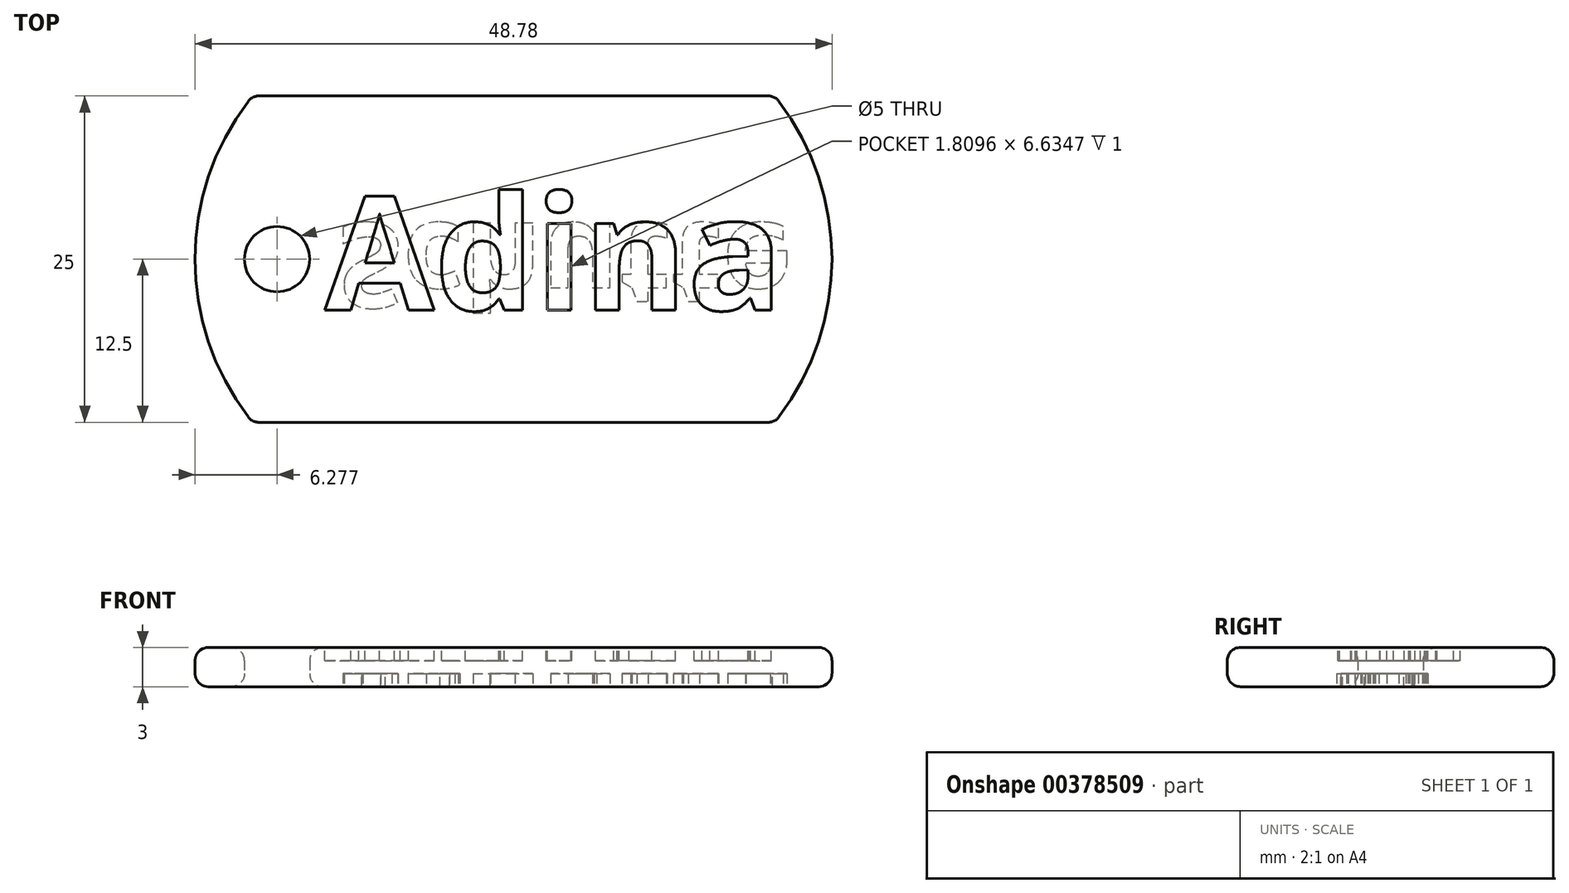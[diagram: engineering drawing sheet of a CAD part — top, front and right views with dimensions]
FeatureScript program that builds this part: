
annotation { "Feature Type Name" : "Feature", "Feature Type Description" : "" }
export const myFeature = defineFeature(function(context is Context, id is Id, definition is map)
    precondition{}
    {
        {
            var Q0;
            Q0=qCreatedBy(makeId("Top.planeOp"),FACE);
            var sketch = newSketch(context, id + "F0", { "sketchPlane" : qUnion([Q0])});
            skLineSegment(sketch, "E0.bottom", {"start": v(-20, 12.5) * mm, "end": v(20, 12.5) * mm});
            skLineSegment(sketch, "E0.top", {"start": v(-20, -12.5) * mm, "end": v(20, -12.5) * mm});
            skArc(sketch, "E1", {"start": v(-20, 12.5) * mm, "mid": v(-24.39, 0) * mm, "end": v(-20, -12.5) * mm});
            skArc(sketch, "E2", {"start": v(20, -12.5) * mm, "mid": v(24.39, 0) * mm, "end": v(20, 12.5) * mm});
            skCircle(sketch, "E3", {"center": v(-18.11, 0) * mm, "radius": 2.5 * mm});
            skSolve(sketch);
        }
        {
            var Q0;
            Q0=makeQuery(id+"F0.imprint","IMPRINT",FACE,{"disambiguationData":[TD([[makeQuery(id+"F0.imprint","IMPRINT",EDGE,{"derivedFrom":sQuery(id+"F0.wireOp",EDGE,"E0.bottom")}),-1.0]])]});
            extrude(context, id + "F1", {"entities" : qUnion([Q0]), "depth" : 3 * mm});
        }
        {
            var Q0;
            Q0=makeQuery(id+"F1.opExtrude","CAP_FACE",FACE,{"disambiguationData":[OSD([sQuery(id+"F0.wireOp",EDGE,"E0.bottom"),sQuery(id+"F0.wireOp",EDGE,"E0.top"),sQuery(id+"F0.wireOp",EDGE,"E1"),sQuery(id+"F0.wireOp",EDGE,"E2"),sQuery(id+"F0.wireOp",EDGE,"E3")])],"isStart":false});
            var sketch = newSketch(context, id + "F2", { "sketchPlane" : qUnion([Q0])});
            skText(sketch, "E4", { "text": "Adina\n", "fontName": "OpenSans-Bold.ttf"});
            const initialGuessF2  = {"E4": [-0.01445, -0.0039, 1, 0, 0.00875]};
            skSetInitialGuess(sketch, initialGuessF2);
            skSolve(sketch);
        }
        {
            var Q0;
            Q0=qSketchRegion(id+"F2",true);
            extrude(context, id + "F3", {"entities" : qUnion([Q0]), "operationType" : NewBodyOperationType.REMOVE, "oppositeDirection" : true, "depth" : 1 * mm});
        }
        {
            var Q0;
            Q0=makeQuery(id+"F1.opExtrude","CAP_FACE",FACE,{"disambiguationData":[OSD([sQuery(id+"F0.wireOp",EDGE,"E0.bottom"),sQuery(id+"F0.wireOp",EDGE,"E0.top"),sQuery(id+"F0.wireOp",EDGE,"E1"),sQuery(id+"F0.wireOp",EDGE,"E2"),sQuery(id+"F0.wireOp",EDGE,"E3")])],"isStart":true});
            var sketch = newSketch(context, id + "F4", { "sketchPlane" : qUnion([Q0])});
            skText(sketch, "E5", { "text": "Schutte", "fontName": "OpenSans-Bold.ttf"});
            const initialGuessF4  = {"E5": [-0.01347, -0.00276, 1, 0, 0.00653]};
            skSetInitialGuess(sketch, initialGuessF4);
            skSolve(sketch);
        }
        {
            var Q0;
            Q0=qSketchRegion(id+"F4",true);
            extrude(context, id + "F5", {"entities" : qUnion([Q0]), "operationType" : NewBodyOperationType.REMOVE, "oppositeDirection" : true, "depth" : 1 * mm});
        }
        {
            var Q0;
            Q0=makeQuery(id+"F1.opExtrude","SWEPT_FACE",FACE,{"disambiguationData":[OSD([sQuery(id+"F0.wireOp",EDGE,"E2")])]});
            var Q1;
            Q1=makeQuery(id+"F1.opExtrude","SWEPT_FACE",FACE,{"disambiguationData":[OSD([sQuery(id+"F0.wireOp",EDGE,"E0.top")])]});
            var Q2;
            Q2=makeQuery(id+"F1.opExtrude","SWEPT_FACE",FACE,{"disambiguationData":[OSD([sQuery(id+"F0.wireOp",EDGE,"E3")])]});
            var Q3;
            Q3=makeQuery(id+"F1.opExtrude","SWEPT_FACE",FACE,{"disambiguationData":[OSD([sQuery(id+"F0.wireOp",EDGE,"E1")])]});
            var Q4;
            Q4=makeQuery(id+"F1.opExtrude","SWEPT_FACE",FACE,{"disambiguationData":[OSD([sQuery(id+"F0.wireOp",EDGE,"E0.bottom")])]});
            fillet(context, id + "F6", {"entities" : qUnion([Q0, Q1, Q2, Q3, Q4]), "radius" : 1 * mm, "tangentPropagation" : true, "allowEdgeOverflow" : false});
        }
    });
